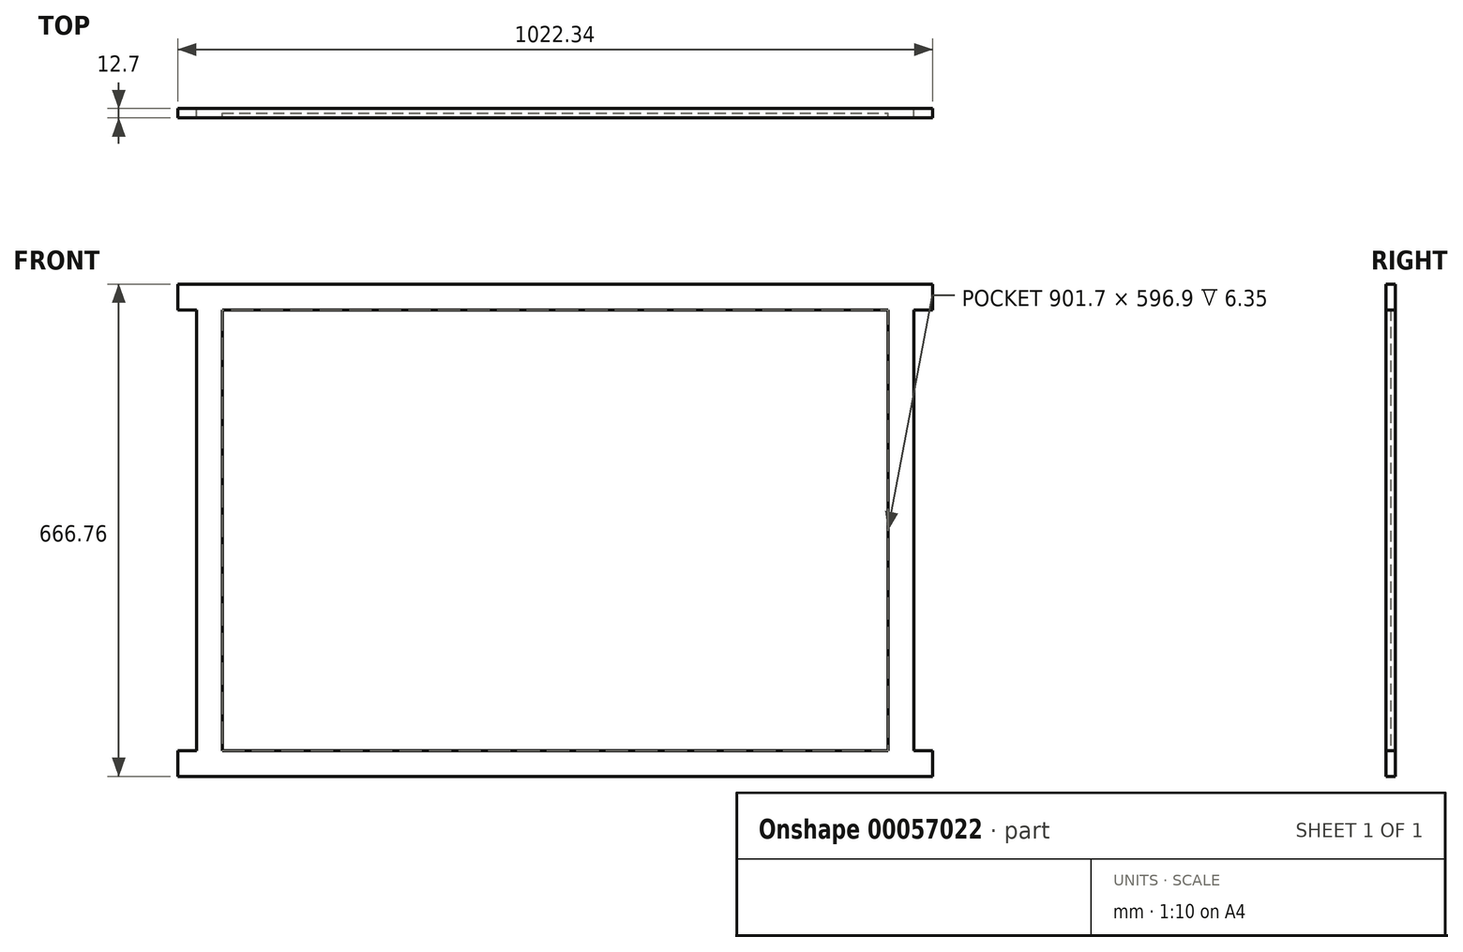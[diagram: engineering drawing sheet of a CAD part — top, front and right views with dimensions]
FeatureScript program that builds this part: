
annotation { "Feature Type Name" : "Feature", "Feature Type Description" : "" }
export const myFeature = defineFeature(function(context is Context, id is Id, definition is map)
    precondition{}
    {
        {
            var Q0;
            Q0=qCreatedBy(makeId("Front.planeOp"),FACE);
            var sketch = newSketch(context, id + "F0", { "sketchPlane" : qUnion([Q0])});
            skLineSegment(sketch, "E0.bottom", {"start": v(-901.7, 298.45) * mm, "end": v(0, 298.45) * mm});
            skLineSegment(sketch, "E0.top", {"start": v(-901.7, -298.45) * mm, "end": v(0, -298.45) * mm});
            skLineSegment(sketch, "E0.left", {"start": v(-901.7, 298.45) * mm, "end": v(-901.7, -298.45) * mm});
            skLineSegment(sketch, "E0.right", {"start": v(0, 298.45) * mm, "end": v(0, -298.45) * mm});
            skLineSegment(sketch, "E1.bottom", {"start": v(-962.03, 333.38) * mm, "end": v(60.33, 333.38) * mm});
            skLineSegment(sketch, "E1.top", {"start": v(-962.03, 298.45) * mm, "end": v(60.33, 298.45) * mm});
            skLineSegment(sketch, "E1.left", {"start": v(-962.03, 333.37) * mm, "end": v(-962.03, 298.45) * mm});
            skLineSegment(sketch, "E1.right", {"start": v(60.33, 333.38) * mm, "end": v(60.33, 298.45) * mm});
            skLineSegment(sketch, "E2.bottom", {"start": v(-962.03, -333.37) * mm, "end": v(60.33, -333.38) * mm});
            skLineSegment(sketch, "E2.top", {"start": v(-962.03, -298.45) * mm, "end": v(60.33, -298.45) * mm});
            skLineSegment(sketch, "E2.left", {"start": v(-962.03, -333.37) * mm, "end": v(-962.03, -298.45) * mm});
            skLineSegment(sketch, "E2.right", {"start": v(60.33, -333.38) * mm, "end": v(60.33, -298.45) * mm});
            skLineSegment(sketch, "E3.bottom", {"start": v(-901.7, 298.45) * mm, "end": v(-936.63, 298.45) * mm});
            skLineSegment(sketch, "E3.top", {"start": v(-901.7, -298.45) * mm, "end": v(-936.63, -298.45) * mm});
            skLineSegment(sketch, "E3.right", {"start": v(-936.63, 298.45) * mm, "end": v(-936.63, -298.45) * mm});
            skLineSegment(sketch, "E4.bottom", {"start": v(0, 298.45) * mm, "end": v(34.93, 298.45) * mm});
            skLineSegment(sketch, "E4.top", {"start": v(0, -298.45) * mm, "end": v(34.93, -298.45) * mm});
            skLineSegment(sketch, "E4.right", {"start": v(34.93, 298.45) * mm, "end": v(34.93, -298.45) * mm});
            skPoint(sketch, "E5.firstSnap0", {"position": v(-962.03, 315.91) * mm});
            skLineSegment(sketch, "E5.bottom", {"start": v(-911.22, 307.98) * mm, "end": v(9.53, 307.98) * mm, "construction": true});
            skLineSegment(sketch, "E5.top", {"start": v(-911.23, -307.97) * mm, "end": v(9.52, -307.98) * mm, "construction": true});
            skLineSegment(sketch, "E5.left", {"start": v(-911.22, 307.98) * mm, "end": v(-911.23, -307.97) * mm, "construction": true});
            skLineSegment(sketch, "E5.right", {"start": v(9.53, 307.98) * mm, "end": v(9.52, -307.98) * mm, "construction": true});
            skPoint(sketch, "E6", {"position": v(-919.16, 298.45) * mm});
            skSolve(sketch);
        }
        {
            var Q0;
            {var subQ0=sQuery(id+"F0.wireOp",EDGE,"E0.left");Q0=makeQuery(id+"F0.imprint","IMPRINT",FACE,{"disambiguationData":[TD([[makeQuery(id+"F0.imprint","IMPRINT",EDGE,{"derivedFrom":subQ0}),1.0]])]});}
            extrude(context, id + "F1", {"entities" : qUnion([Q0]), "depth" : 6.35 * mm});
        }
        {
            var Q0;
            Q0 = qSketchRegion(id + "F0", true);
            extrude(context, id + "F2", {"entities" : qUnion([Q0]), "operationType" : NewBodyOperationType.ADD, "depth" : 12.7 * mm});
        }
    });
